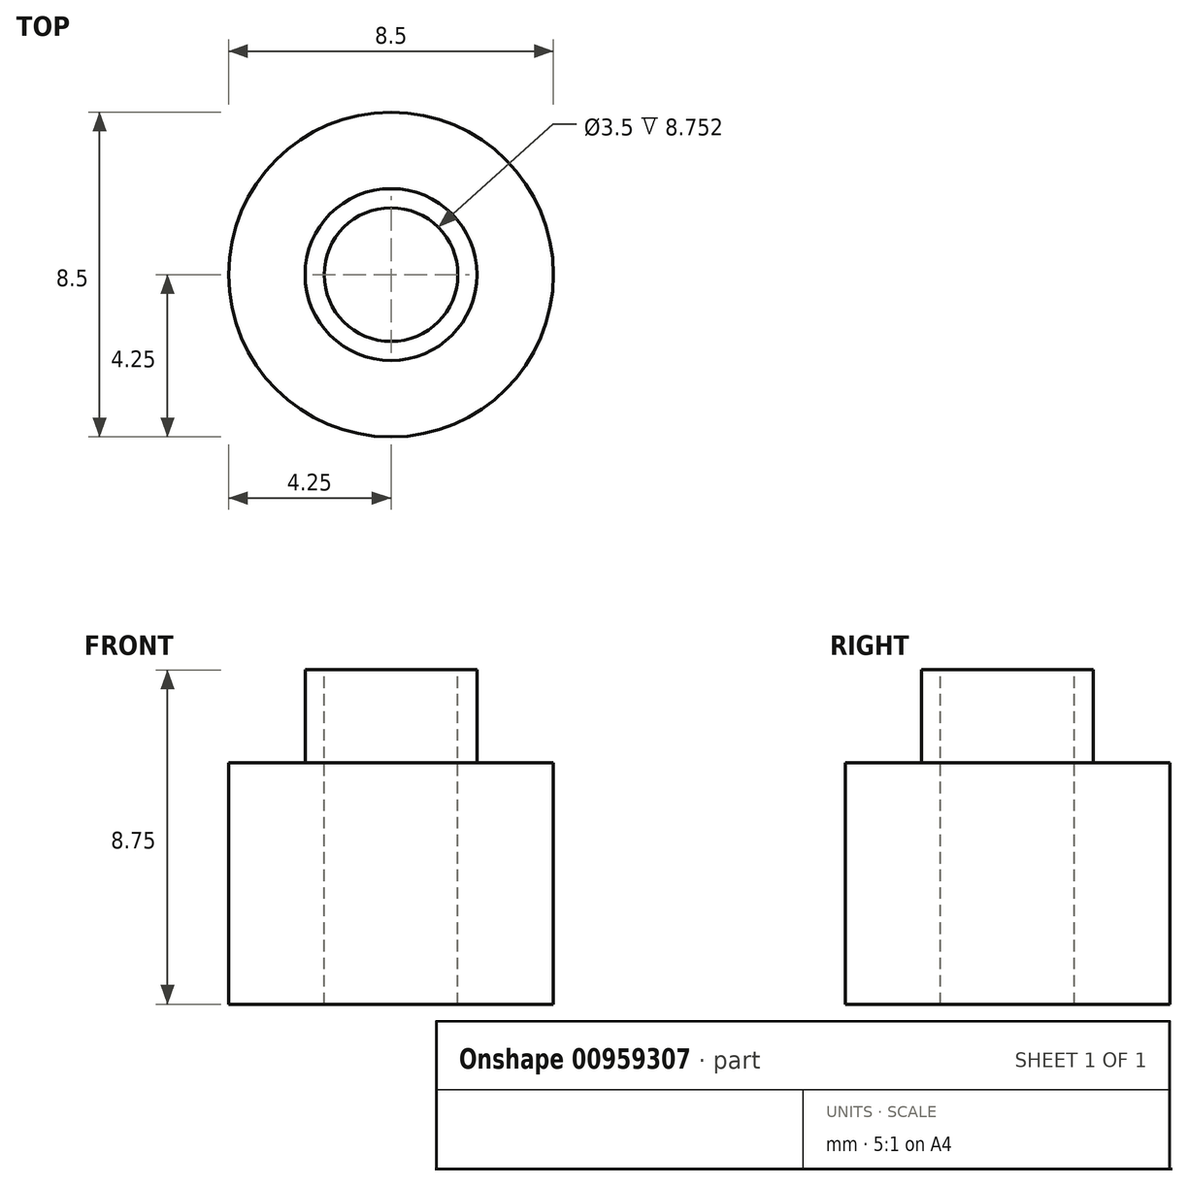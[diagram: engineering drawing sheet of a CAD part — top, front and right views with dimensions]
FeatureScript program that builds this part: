
annotation { "Feature Type Name" : "Feature", "Feature Type Description" : "" }
export const myFeature = defineFeature(function(context is Context, id is Id, definition is map)
    precondition{}
    {
        {
            var Q0;
            Q0=qCreatedBy(makeId("Front.planeOp"),FACE);
            var sketch = newSketch(context, id + "F0", { "sketchPlane" : qUnion([Q0])});
            skLineSegment(sketch, "E0", {"start": v(0, 0) * mm, "end": v(0, -6.32) * mm});
            skLineSegment(sketch, "E1", {"start": v(0, -6.32) * mm, "end": v(-2.5, -6.32) * mm});
            skLineSegment(sketch, "E2", {"start": v(-2.5, -6.32) * mm, "end": v(-2.5, 0) * mm});
            skLineSegment(sketch, "E3", {"start": v(-2.5, 0) * mm, "end": v(-0.5, 0) * mm});
            skPoint(sketch, "E3.endSnap0", {"position": v(-0.5, -6.32) * mm});
            skLineSegment(sketch, "E4", {"start": v(-0.5, 0) * mm, "end": v(-0.5, 2.43) * mm});
            skLineSegment(sketch, "E5", {"start": v(-0.5, 2.43) * mm, "end": v(0, 2.43) * mm});
            skLineSegment(sketch, "E6", {"start": v(0, 2.43) * mm, "end": v(0, 0) * mm});
            skLineSegment(sketch, "E7", {"start": v(1.75, 4.4) * mm, "end": v(1.75, -10.88) * mm, "construction": true});
            skSolve(sketch);
        }
        {
            var Q0;
            Q0=makeQuery(id+"F0.imprint","IMPRINT",FACE,{"disambiguationData":[TD([[makeQuery(id+"F0.imprint","IMPRINT",EDGE,{"derivedFrom":sQuery(id+"F0.wireOp",EDGE,"E0")}),-1.0]])]});
            var Q1;
            Q1=sQuery(id+"F0.wireOp",EDGE,"E7");
            revolve(context, id + "F1", {"surfaceOperationType" : NewSurfaceOperationType.NEW, "entities" : qUnion([Q0]), "axis" : qUnion([Q1]), "revolveType" : RevolveType.FULL});
        }
    });
